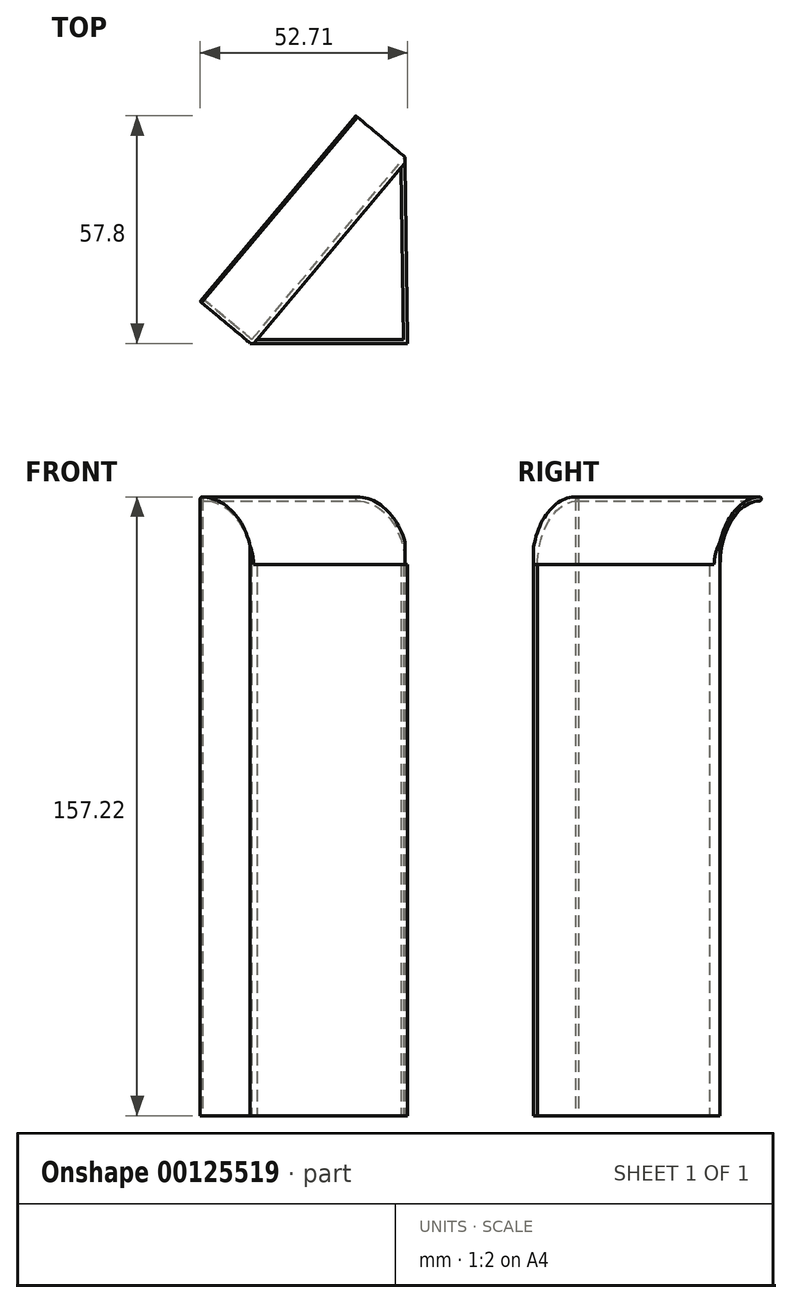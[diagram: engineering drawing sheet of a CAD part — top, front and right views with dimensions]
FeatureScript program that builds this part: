
annotation { "Feature Type Name" : "Feature", "Feature Type Description" : "" }
export const myFeature = defineFeature(function(context is Context, id is Id, definition is map)
    precondition{}
    {
        {
            var Q0;
            Q0=qCreatedBy(makeId("Top.planeOp"),FACE);
            var sketch = newSketch(context, id + "F0", { "sketchPlane" : qUnion([Q0])});
            skLineSegment(sketch, "E0.bottom", {"start": v(0, 0) * mm, "end": v(-40, 0) * mm});
            skLineSegment(sketch, "E0.top", {"start": v(0, 1) * mm, "end": v(-0.02, 1) * mm});
            skLineSegment(sketch, "E0.left", {"start": v(0, 0) * mm, "end": v(0, 1) * mm});
            skLineSegment(sketch, "E1", {"start": v(-40, 0) * mm, "end": v(-52.7, 10.66) * mm});
            skLineSegment(sketch, "E2", {"start": v(-52.7, 10.66) * mm, "end": v(-52.06, 11.43) * mm});
            skLineSegment(sketch, "E3", {"start": v(-52.06, 11.43) * mm, "end": v(-39.64, 1) * mm});
            skLineSegment(sketch, "E4", {"start": v(0, 0) * mm, "end": v(-0.72, 47.37) * mm});
            skLineSegment(sketch, "E5", {"start": v(-1.1, 72) * mm, "end": v(-2.1, 71.98) * mm});
            skLineSegment(sketch, "E6", {"start": v(-1.68, 44.68) * mm, "end": v(-1.02, 1) * mm});
            skLineSegment(sketch, "E7.trimOffspring", {"start": v(-1.02, 1) * mm, "end": v(-38.33, 1) * mm});
            skLineSegment(sketch, "E8", {"start": v(-39.64, 1) * mm, "end": v(-0.72, 47.37) * mm});
            skLineSegment(sketch, "E9", {"start": v(27.73, 81.29) * mm, "end": v(28.5, 80.64) * mm});
            skLineSegment(sketch, "E10", {"start": v(-1.68, 44.68) * mm, "end": v(-38.33, 1) * mm});
            skSolve(sketch);
        }
        {
            var Q0;
            Q0 = qSketchRegion(id + "F0", true);
            extrude(context, id + "F1", {"entities" : qUnion([Q0]), "depth" : 140 * mm});
        }
        {
            var Q0;
            Q0=makeQuery(id+"F1.opExtrude","SWEPT_FACE",FACE,{"disambiguationData":[OSD([sQuery(id+"F0.wireOp",EDGE,"E3")])]});
            cPlane(context, id + "F2", {"entities" : qUnion([Q0]), "cplaneType" : CPlaneType.OFFSET, "offset" : 60.54 * mm, "width" : 150 * mm, "height" : 150 * mm});
        }
        {
            var Q0;
            Q0=qCreatedBy(id+"F2.planeOp",FACE);
            var sketch = newSketch(context, id + "F3", { "sketchPlane" : qUnion([Q0])});
            skPoint(sketch, "E11.0", {"position": v(30, 140) * mm});
            skPoint(sketch, "E11.1", {"position": v(31, 140) * mm});
            skLineSegment(sketch, "E12", {"start": v(56.91, 151.7) * mm, "end": v(56.25, 150.95) * mm, "construction": true});
            skLineSegment(sketch, "E13", {"start": v(31, 140) * mm, "end": v(30, 140) * mm});
            skLineSegment(sketch, "E14", {"start": v(47.23, 156.22) * mm, "end": v(47.23, 156.73) * mm, "construction": true});
            skArc(sketch, "E15", {"start": v(46.76, 156.22) * mm, "mid": v(35.6, 151.3) * mm, "end": v(31, 140) * mm});
            skArc(sketch, "E16", {"start": v(46.73, 157.22) * mm, "mid": v(34.88, 152) * mm, "end": v(30, 140) * mm});
            skPoint(sketch, "E17", {"position": v(47.23, 156.22) * mm});
            skPoint(sketch, "E18", {"position": v(47.23, 156.72) * mm});
            skLineSegment(sketch, "E19", {"start": v(64.45, 140) * mm, "end": v(63.95, 140) * mm, "construction": true});
            skPoint(sketch, "E20", {"position": v(63.95, 140) * mm});
            skArc(sketch, "E21", {"start": v(47.23, 156.72) * mm, "mid": v(35.4, 151.83) * mm, "end": v(30.5, 140) * mm, "construction": true});
            skPoint(sketch, "E22", {"position": v(46.73, 156.72) * mm});
            skArc(sketch, "E23", {"start": v(46.73, 156.22) * mm, "mid": v(47.23, 156.72) * mm, "end": v(46.73, 157.22) * mm});
            skPoint(sketch, "E24.orphan", {"position": v(63.45, 140) * mm});
            skSolve(sketch);
        }
        {
            var Q0;
            Q0 = qSketchRegion(id + "F3", true);
            var Q1;
            Q1=makeQuery(id+"F1.opExtrude","SWEPT_FACE",FACE,{"disambiguationData":[OSD([sQuery(id+"F0.wireOp",EDGE,"E1")])]});
            var Q2;
            Q2=makeQuery(id+"F1.opExtrude","SWEPT_BODY",BODY,{"disambiguationData":[OSD([sQuery(id+"F0.wireOp",EDGE,"E0.bottom"),sQuery(id+"F0.wireOp",EDGE,"E0.top"),sQuery(id+"F0.wireOp",EDGE,"E0.left"),sQuery(id+"F0.wireOp",EDGE,"E1"),sQuery(id+"F0.wireOp",EDGE,"E2"),sQuery(id+"F0.wireOp",EDGE,"E3"),sQuery(id+"F0.wireOp",EDGE,"E4"),sQuery(id+"F0.wireOp",EDGE,"E6"),sQuery(id+"F0.wireOp",EDGE,"E7.trimOffspring"),sQuery(id+"F0.wireOp",EDGE,"E8"),sQuery(id+"F0.wireOp",EDGE,"E10")])]});
            extrude(context, id + "F4", {"entities" : qUnion([Q0]), "operationType" : NewBodyOperationType.ADD, "endBound" : BoundingType.UP_TO_SURFACE, "oppositeDirection" : true, "endBoundEntityFace" : qUnion([Q1]), "endBoundEntityBody" : qUnion([Q2]), "depth" : 25 * mm});
        }
        {
            var Q0;
            {var subQ0=sQuery(id+"F0.wireOp",EDGE,"E1");Q0=makeQuery(id+"F4.boolean.opBoolean","MERGE",FACE,{"derivedFrom":[makeQuery(id+"F1.opExtrude","SWEPT_FACE",FACE,{"disambiguationData":[OSD([subQ0])]}),makeQuery(id+"F4.opExtrude","CAP_FACE",FACE,{"disambiguationData":[OSD([subQ0])],"isStart":false})]});}
            var sketch = newSketch(context, id + "F5", { "sketchPlane" : qUnion([Q0])});
            skLineSegment(sketch, "E25.0", {"start": v(-31, 140) * mm, "end": v(-47.23, 140) * mm});
            skArc(sketch, "E25.1", {"start": v(-46.73, 156.22) * mm, "mid": v(-35.58, 151.3) * mm, "end": v(-31, 140) * mm});
            skLineSegment(sketch, "E26", {"start": v(-47.23, 140) * mm, "end": v(-47.23, 156.73) * mm});
            skArc(sketch, "E27.0", {"start": v(-46.73, 156.22) * mm, "mid": v(-47.23, 156.72) * mm, "end": v(-46.73, 157.22) * mm});
            skSolve(sketch);
        }
        {
            var Q0;
            Q0 = qSketchRegion(id + "F5", true);
            extrude(context, id + "F6", {"entities" : qUnion([Q0]), "operationType" : NewBodyOperationType.ADD, "oppositeDirection" : true, "depth" : 1 * mm});
        }
        {
            var Q0;
            {var subQ1=sQuery(id+"F0.wireOp",EDGE,"E0.bottom");Q0=makeQuery(id+"F4.boolean.opBoolean","SPLIT",FACE,{"disambiguationData":[TD([makeQuery(id+"F1.opExtrude","SWEPT_FACE",FACE,{"disambiguationData":[OSD([subQ1])]})])],"derivedFrom":makeQuery(id+"F4.opExtrude","SWEPT_FACE",FACE,{"disambiguationData":[OSD([sQuery(id+"F3.wireOp",EDGE,"E13")])]})});}
            var sketch = newSketch(context, id + "F7", { "sketchPlane" : qUnion([Q0])});
            skLineSegment(sketch, "E28.0", {"start": v(-39.17, 0) * mm, "end": v(-40, 0) * mm});
            skLineSegment(sketch, "E28.1", {"start": v(-40, 0) * mm, "end": v(-39.51, 0.4) * mm});
            skLineSegment(sketch, "E28.2", {"start": v(-39.51, 0.4) * mm, "end": v(-39.17, 0) * mm});
            skSolve(sketch);
        }
        {
            var Q0;
            Q0 = qSketchRegion(id + "F7", true);
            extrude(context, id + "F8", {"entities" : qUnion([Q0]), "operationType" : NewBodyOperationType.REMOVE, "oppositeDirection" : true, "depth" : 10 * mm});
        }
        {
            var Q0;
            {var subQ2=sQuery(id+"F3.wireOp",EDGE,"E13");var subQ4=sQuery(id+"F0.wireOp",EDGE,"E4");Q0=makeQuery(id+"F4.boolean.opBoolean","SPLIT",FACE,{"disambiguationData":[TD([makeQuery(id+"F1.opExtrude","SWEPT_FACE",FACE,{"disambiguationData":[OSD([subQ4])]})])],"derivedFrom":makeQuery(id+"F4.opExtrude","SWEPT_FACE",FACE,{"disambiguationData":[OSD([subQ2])]})});}
            var sketch = newSketch(context, id + "F9", { "sketchPlane" : qUnion([Q0])});
            skLineSegment(sketch, "E29.0", {"start": v(-0.72, -47.37) * mm, "end": v(0.04, -46.73) * mm});
            skLineSegment(sketch, "E29.1", {"start": v(-0.7, -45.85) * mm, "end": v(0.04, -46.73) * mm});
            skLineSegment(sketch, "E29.2", {"start": v(-0.7, -45.85) * mm, "end": v(-0.72, -47.37) * mm});
            skSolve(sketch);
        }
        {
            var Q0;
            Q0=makeQuery(id+"F9.imprint","IMPRINT",FACE,{"disambiguationData":[TD([[makeQuery(id+"F9.imprint","IMPRINT",EDGE,{"derivedFrom":sQuery(id+"F9.wireOp",EDGE,"E29.0")}),1.0]])]});
            extrude(context, id + "F10", {"entities" : qUnion([Q0]), "operationType" : NewBodyOperationType.REMOVE, "oppositeDirection" : true, "depth" : 25 * mm});
        }
    });
